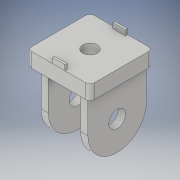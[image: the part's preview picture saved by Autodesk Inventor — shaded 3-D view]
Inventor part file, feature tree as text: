
AUTODESK INVENTOR PART (.ipt)
format: ipt  version: 2018 (Build 220112000, 112)  size: 190,976 bytes
history: native  units: mm
features: sketch x6, extrude x5, projected_geometry x2, hole x1
ambient origin geometry x8: Origin, YZ Plane, XZ Plane, XY Plane, X Axis, Y Axis, Z Axis, Center Point
bodies: Volumenkörper1 (feature_tree), Volumenkörper2 (feature_tree)
feature tree (14):
  extrude  "Extrusion1"  Depth=3.0mm
  extrude  "Extrusion2"  Depth=0.7mm
  extrude  "Extrusion3"  Depth=0.6mm
  extrude  "Extrusion4"  Depth=0.6mm
  extrude  "Extrusion5"  Depth=0.6mm
  hole  "Bohrung1"  [1 undecoded]
  sketch  "Skizze1"  dims[d0=3.0mm d1=3.0mm]
  sketch  "Skizze2"  dims[d2=0.2mm d3=0.7mm]
  projected_geometry  "Projizierte Kontur1"
  sketch  "Skizze3"  dims[d4=0.7mm d5=0.0mm d6=0.6mm]
  projected_geometry  "Projizierte Kontur2"
  sketch  "Skizze4"  dims[d7=0.1mm d8=0.6mm]
  sketch  "Skizze5"  dims[d9=0.6mm d10=0.6mm]
  sketch  "Skizze6"  dims[d11=0.1mm d12=0.1mm d13=0.1mm d14=0.25mm d15=0.0mm d16=0.35mm d17=0.35mm d18=2.8mm d19=0.2mm d20=0.55mm d21=1.55mm d22=0.0mm d23=0.35mm d24=0.0mm d25=0.35mm d26=0.0mm d27=0.8mm d28=6.0mm d29=4.0mm d30=2.0mm d31=90.0deg d32=8.0mm d33=20.594885mm]
note: 1 required parameter value undecoded (feature->parameter linkage not recoverable at this tier; creation-order binding heuristic only, values carry confidence <= 0.55)
